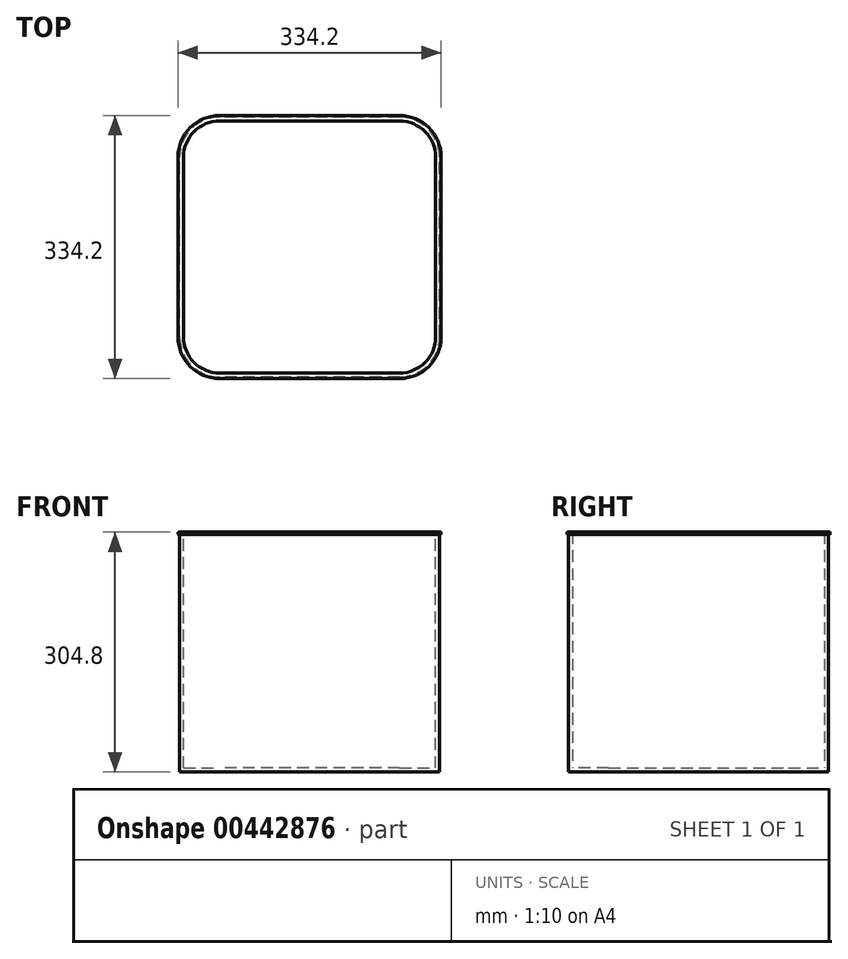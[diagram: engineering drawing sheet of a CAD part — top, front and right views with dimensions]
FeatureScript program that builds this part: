
annotation { "Feature Type Name" : "Feature", "Feature Type Description" : "" }
export const myFeature = defineFeature(function(context is Context, id is Id, definition is map)
    precondition{}
    {
        {
            var Q0;
            Q0=qCreatedBy(makeId("Top.planeOp"),FACE);
            var sketch = newSketch(context, id + "F0", { "sketchPlane" : qUnion([Q0])});
            skLineSegment(sketch, "E0.bottom", {"start": v(165.1, -165.1) * mm, "end": v(-165.1, -165.1) * mm});
            skLineSegment(sketch, "E0.top", {"start": v(165.1, 165.1) * mm, "end": v(-165.1, 165.1) * mm});
            skLineSegment(sketch, "E0.left", {"start": v(165.1, -165.1) * mm, "end": v(165.1, 165.1) * mm});
            skLineSegment(sketch, "E0.right", {"start": v(-165.1, -165.1) * mm, "end": v(-165.1, 165.1) * mm});
            skPoint(sketch, "E0.middle", {"position": v(0, 0) * mm});
            skSolve(sketch);
        }
        {
            var Q0;
            Q0 = qSketchRegion(id + "F0", true);
            extrude(context, id + "F1", {"entities" : qUnion([Q0]), "depth" : 304.8 * mm});
        }
        {
            var Q0;
            Q0=makeQuery(id+"F1.opExtrude","SWEPT_EDGE",EDGE,{"disambiguationData":[OSD([sQuery(id+"F0.wireOp",EDGE,"E0.bottom"),sQuery(id+"F0.wireOp",EDGE,"E0.right")])]});
            var Q1;
            Q1=makeQuery(id+"F1.opExtrude","SWEPT_EDGE",EDGE,{"disambiguationData":[OSD([sQuery(id+"F0.wireOp",EDGE,"E0.bottom"),sQuery(id+"F0.wireOp",EDGE,"E0.left")])]});
            var Q2;
            Q2=makeQuery(id+"F1.opExtrude","SWEPT_EDGE",EDGE,{"disambiguationData":[OSD([sQuery(id+"F0.wireOp",EDGE,"E0.top"),sQuery(id+"F0.wireOp",EDGE,"E0.left")])]});
            var Q3;
            Q3=makeQuery(id+"F1.opExtrude","SWEPT_EDGE",EDGE,{"disambiguationData":[OSD([sQuery(id+"F0.wireOp",EDGE,"E0.top"),sQuery(id+"F0.wireOp",EDGE,"E0.right")])]});
            fillet(context, id + "F2", {"entities" : qUnion([Q0, Q1, Q2, Q3]), "radius" : 50.8 * mm, "tangentPropagation" : true, "allowEdgeOverflow" : false});
        }
        {
            var Q0;
            Q0=makeQuery(id+"F1.opExtrude","CAP_FACE",FACE,{"disambiguationData":[OSD([sQuery(id+"F0.wireOp",EDGE,"E0.bottom"),sQuery(id+"F0.wireOp",EDGE,"E0.top"),sQuery(id+"F0.wireOp",EDGE,"E0.left"),sQuery(id+"F0.wireOp",EDGE,"E0.right")])],"isStart":false});
            shell(context, id + "F3", {"entities" : qUnion([Q0]), "thickness" : 5 * mm});
        }
        {
            var Q0;
            Q0=makeQuery(id+"F1.opExtrude","CAP_FACE",FACE,{"disambiguationData":[OSD([sQuery(id+"F0.wireOp",EDGE,"E0.bottom"),sQuery(id+"F0.wireOp",EDGE,"E0.top"),sQuery(id+"F0.wireOp",EDGE,"E0.left"),sQuery(id+"F0.wireOp",EDGE,"E0.right")])],"isStart":false});
            var sketch = newSketch(context, id + "F4", { "sketchPlane" : qUnion([Q0])});
            skLineSegment(sketch, "E1.0", {"start": v(-165.1, -114.3) * mm, "end": v(-165.1, 114.3) * mm});
            skArc(sketch, "E2.0", {"start": v(-114.3, 165.1) * mm, "mid": v(-150.22, 150.22) * mm, "end": v(-165.1, 114.3) * mm});
            skLineSegment(sketch, "E3.0", {"start": v(114.3, 165.1) * mm, "end": v(-114.3, 165.1) * mm});
            skArc(sketch, "E4.0", {"start": v(165.1, 114.3) * mm, "mid": v(150.22, 150.22) * mm, "end": v(114.3, 165.1) * mm});
            skLineSegment(sketch, "E5.0", {"start": v(165.1, -114.3) * mm, "end": v(165.1, 114.3) * mm});
            skPoint(sketch, "E6.0", {"position": v(150.22, -150.22) * mm});
            skLineSegment(sketch, "E7.0", {"start": v(114.3, -165.1) * mm, "end": v(-114.3, -165.1) * mm});
            skArc(sketch, "E8.0", {"start": v(-165.1, -114.3) * mm, "mid": v(-150.22, -150.22) * mm, "end": v(-114.3, -165.1) * mm});
            skArc(sketch, "E9.0", {"start": v(114.3, -165.1) * mm, "mid": v(150.22, -150.22) * mm, "end": v(165.1, -114.3) * mm});
            skArc(sketch, "E10.0", {"start": v(114.3, -167.1) * mm, "mid": v(151.64, -151.64) * mm, "end": v(167.1, -114.3) * mm});
            skLineSegment(sketch, "E10.1", {"start": v(114.3, -167.1) * mm, "end": v(-114.3, -167.1) * mm});
            skLineSegment(sketch, "E10.2", {"start": v(167.1, -114.3) * mm, "end": v(167.1, 114.3) * mm});
            skArc(sketch, "E10.3", {"start": v(-167.1, -114.3) * mm, "mid": v(-151.64, -151.64) * mm, "end": v(-114.3, -167.1) * mm});
            skArc(sketch, "E10.4", {"start": v(167.1, 114.3) * mm, "mid": v(151.64, 151.64) * mm, "end": v(114.3, 167.1) * mm});
            skLineSegment(sketch, "E10.5", {"start": v(114.3, 167.1) * mm, "end": v(-114.3, 167.1) * mm});
            skArc(sketch, "E10.6", {"start": v(-114.3, 167.1) * mm, "mid": v(-151.64, 151.64) * mm, "end": v(-167.1, 114.3) * mm});
            skLineSegment(sketch, "E10.7", {"start": v(-167.1, -114.3) * mm, "end": v(-167.1, 114.3) * mm});
            skSolve(sketch);
        }
        {
            var Q0;
            Q0 = qSketchRegion(id + "F4", true);
            extrude(context, id + "F5", {"entities" : qUnion([Q0]), "operationType" : NewBodyOperationType.ADD, "oppositeDirection" : true, "depth" : 3 * mm});
        }
        {
            var Q0;
            Q0=makeQuery(id+"F5.opExtrude","CAP_EDGE",EDGE,{"disambiguationData":[OSD([sQuery(id+"F4.wireOp",EDGE,"E10.3")])],"isStart":false});
            var Q1;
            Q1=makeQuery(id+"F5.opExtrude","CAP_EDGE",EDGE,{"disambiguationData":[OSD([sQuery(id+"F4.wireOp",EDGE,"E10.3")])],"isStart":true});
            var Q2;
            Q2=makeQuery(id+"F5.opExtrude","CAP_EDGE",EDGE,{"disambiguationData":[OSD([sQuery(id+"F4.wireOp",EDGE,"E10.1")])],"isStart":true});
            var Q3;
            Q3=makeQuery(id+"F5.opExtrude","CAP_EDGE",EDGE,{"disambiguationData":[OSD([sQuery(id+"F4.wireOp",EDGE,"E10.1")])],"isStart":false});
            var Q4;
            Q4=makeQuery(id+"F5.opExtrude","CAP_EDGE",EDGE,{"disambiguationData":[OSD([sQuery(id+"F4.wireOp",EDGE,"E10.7")])],"isStart":false});
            var Q5;
            Q5=makeQuery(id+"F5.opExtrude","CAP_EDGE",EDGE,{"disambiguationData":[OSD([sQuery(id+"F4.wireOp",EDGE,"E10.7")])],"isStart":true});
            var Q6;
            Q6=makeQuery(id+"F5.opExtrude","CAP_EDGE",EDGE,{"disambiguationData":[OSD([sQuery(id+"F4.wireOp",EDGE,"E10.6")])],"isStart":true});
            var Q7;
            Q7=makeQuery(id+"F5.opExtrude","CAP_EDGE",EDGE,{"disambiguationData":[OSD([sQuery(id+"F4.wireOp",EDGE,"E10.5")])],"isStart":true});
            var Q8;
            Q8=makeQuery(id+"F5.opExtrude","CAP_EDGE",EDGE,{"disambiguationData":[OSD([sQuery(id+"F4.wireOp",EDGE,"E10.5")])],"isStart":false});
            var Q9;
            Q9=makeQuery(id+"F5.opExtrude","CAP_EDGE",EDGE,{"disambiguationData":[OSD([sQuery(id+"F4.wireOp",EDGE,"E10.6")])],"isStart":false});
            var Q10;
            Q10=makeQuery(id+"F5.opExtrude","CAP_EDGE",EDGE,{"disambiguationData":[OSD([sQuery(id+"F4.wireOp",EDGE,"E10.4")])],"isStart":true});
            var Q11;
            Q11=makeQuery(id+"F5.opExtrude","CAP_EDGE",EDGE,{"disambiguationData":[OSD([sQuery(id+"F4.wireOp",EDGE,"E10.4")])],"isStart":false});
            var Q12;
            Q12=makeQuery(id+"F5.opExtrude","CAP_EDGE",EDGE,{"disambiguationData":[OSD([sQuery(id+"F4.wireOp",EDGE,"E4.0")])],"isStart":false});
            var Q13;
            Q13=makeQuery(id+"F5.opExtrude","CAP_EDGE",EDGE,{"disambiguationData":[OSD([sQuery(id+"F4.wireOp",EDGE,"E10.2")])],"isStart":false});
            var Q14;
            Q14=makeQuery(id+"F5.opExtrude","CAP_EDGE",EDGE,{"disambiguationData":[OSD([sQuery(id+"F4.wireOp",EDGE,"E10.2")])],"isStart":true});
            var Q15;
            Q15=makeQuery(id+"F5.opExtrude","CAP_EDGE",EDGE,{"disambiguationData":[OSD([sQuery(id+"F4.wireOp",EDGE,"E5.0")])],"isStart":false});
            var Q16;
            Q16=makeQuery(id+"F5.opExtrude","CAP_EDGE",EDGE,{"disambiguationData":[OSD([sQuery(id+"F4.wireOp",EDGE,"E3.0")])],"isStart":false});
            var Q17;
            Q17=makeQuery(id+"F5.opExtrude","CAP_EDGE",EDGE,{"disambiguationData":[OSD([sQuery(id+"F4.wireOp",EDGE,"E2.0")])],"isStart":false});
            var Q18;
            Q18=makeQuery(id+"F5.opExtrude","CAP_EDGE",EDGE,{"disambiguationData":[OSD([sQuery(id+"F4.wireOp",EDGE,"E1.0")])],"isStart":false});
            var Q19;
            Q19=makeQuery(id+"F5.opExtrude","CAP_EDGE",EDGE,{"disambiguationData":[OSD([sQuery(id+"F4.wireOp",EDGE,"E10.0")])],"isStart":false});
            var Q20;
            Q20=makeQuery(id+"F5.opExtrude","CAP_EDGE",EDGE,{"disambiguationData":[OSD([sQuery(id+"F4.wireOp",EDGE,"E10.0")])],"isStart":true});
            var Q21;
            Q21=makeQuery(id+"F5.opExtrude","CAP_EDGE",EDGE,{"disambiguationData":[OSD([sQuery(id+"F4.wireOp",EDGE,"E9.0")])],"isStart":false});
            var Q22;
            Q22=makeQuery(id+"F5.opExtrude","CAP_EDGE",EDGE,{"disambiguationData":[OSD([sQuery(id+"F4.wireOp",EDGE,"E7.0")])],"isStart":false});
            fillet(context, id + "F6", {"entities" : qUnion([Q0, Q1, Q2, Q3, Q4, Q5, Q6, Q7, Q8, Q9, Q10, Q11, Q12, Q13, Q14, Q15, Q16, Q17, Q18, Q19, Q20, Q21, Q22]), "radius" : 1 * mm, "tangentPropagation" : true, "allowEdgeOverflow" : false});
        }
    });
